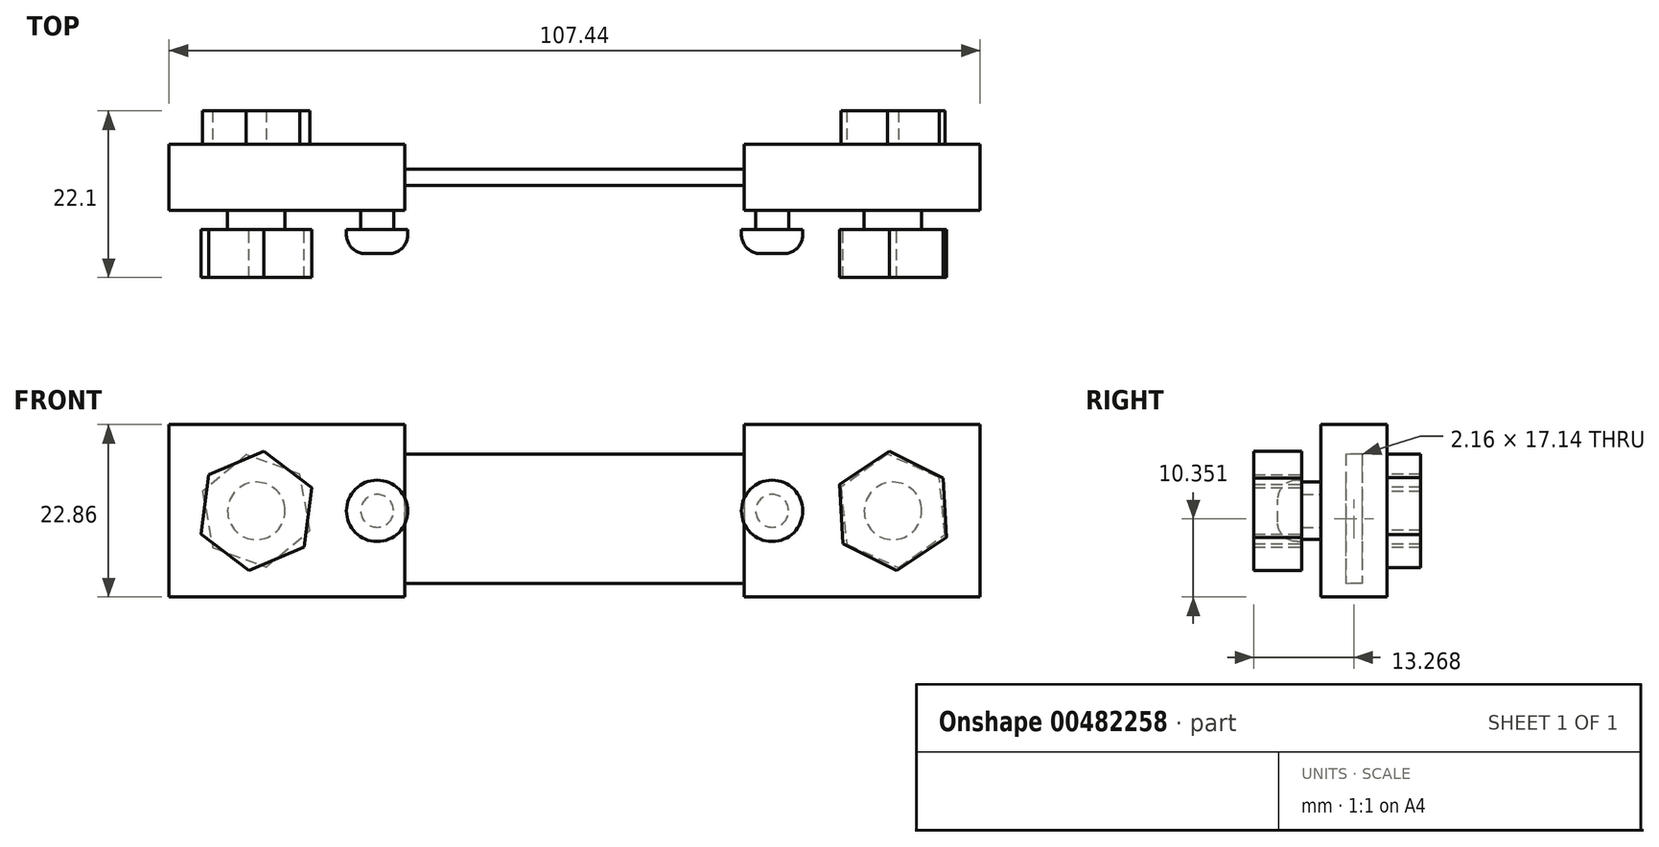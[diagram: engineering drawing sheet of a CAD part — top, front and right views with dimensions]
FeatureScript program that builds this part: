
annotation { "Feature Type Name" : "Feature", "Feature Type Description" : "" }
export const myFeature = defineFeature(function(context is Context, id is Id, definition is map)
    precondition{}
    {
        {
            var Q0;
            Q0=qCreatedBy(makeId("Front.planeOp"),FACE);
            var sketch = newSketch(context, id + "F0", { "sketchPlane" : qUnion([Q0])});
            skLineSegment(sketch, "E0.bottom", {"start": v(-53.72, 11.43) * mm, "end": v(53.72, 11.43) * mm});
            skLineSegment(sketch, "E0.top", {"start": v(-53.72, -11.43) * mm, "end": v(53.72, -11.43) * mm});
            skLineSegment(sketch, "E0.left", {"start": v(-53.72, 11.43) * mm, "end": v(-53.72, -11.43) * mm});
            skLineSegment(sketch, "E0.right", {"start": v(53.72, 11.43) * mm, "end": v(53.72, -11.43) * mm});
            skPoint(sketch, "E0.middle", {"position": v(0, 0) * mm});
            skSolve(sketch);
        }
        {
            var Q0;
            Q0 = qSketchRegion(id + "F0", true);
            extrude(context, id + "F1", {"entities" : qUnion([Q0]), "depth" : 8.76 * mm});
        }
        {
            var Q0;
            Q0=makeQuery(id+"F1.opExtrude","CAP_FACE",FACE,{"disambiguationData":[OSD([sQuery(id+"F0.wireOp",EDGE,"E0.bottom"),sQuery(id+"F0.wireOp",EDGE,"E0.top"),sQuery(id+"F0.wireOp",EDGE,"E0.left"),sQuery(id+"F0.wireOp",EDGE,"E0.right")])],"isStart":false});
            var sketch = newSketch(context, id + "F2", { "sketchPlane" : qUnion([Q0])});
            skLineSegment(sketch, "E1.bottom", {"start": v(22.48, 7.5) * mm, "end": v(-22.48, 7.5) * mm});
            skLineSegment(sketch, "E1.top", {"start": v(22.48, 14.3) * mm, "end": v(-22.48, 14.3) * mm});
            skLineSegment(sketch, "E1.left", {"start": v(22.48, 7.5) * mm, "end": v(22.48, 14.3) * mm});
            skLineSegment(sketch, "E1.right", {"start": v(-22.48, 7.5) * mm, "end": v(-22.48, 14.3) * mm});
            skPoint(sketch, "E1.middle", {"position": v(0, 10.9) * mm});
            skLineSegment(sketch, "E2.bottom", {"start": v(22.48, -9.65) * mm, "end": v(-22.48, -9.65) * mm});
            skLineSegment(sketch, "E2.top", {"start": v(22.48, -16.45) * mm, "end": v(-22.48, -16.45) * mm});
            skLineSegment(sketch, "E2.left", {"start": v(22.48, -9.65) * mm, "end": v(22.48, -16.45) * mm});
            skLineSegment(sketch, "E2.right", {"start": v(-22.48, -9.65) * mm, "end": v(-22.48, -16.45) * mm});
            skPoint(sketch, "E2.middle", {"position": v(0, -13.05) * mm});
            skLineSegment(sketch, "E3", {"start": v(-22.48, 7.5) * mm, "end": v(-22.48, -9.65) * mm, "construction": true});
            skSolve(sketch);
        }
        {
            var Q0;
            Q0 = qSketchRegion(id + "F2", true);
            extrude(context, id + "F3", {"entities" : qUnion([Q0]), "operationType" : NewBodyOperationType.REMOVE, "oppositeDirection" : true, "depth" : 25.4 * mm});
        }
        {
            var Q0;
            Q0=makeQuery(id+"F1.opExtrude","CAP_FACE",FACE,{"disambiguationData":[OSD([sQuery(id+"F0.wireOp",EDGE,"E0.bottom"),sQuery(id+"F0.wireOp",EDGE,"E0.top"),sQuery(id+"F0.wireOp",EDGE,"E0.left"),sQuery(id+"F0.wireOp",EDGE,"E0.right")])],"isStart":false});
            var sketch = newSketch(context, id + "F4", { "sketchPlane" : qUnion([Q0])});
            skLineSegment(sketch, "E4.bottom", {"start": v(-22.48, 7.5) * mm, "end": v(22.48, 7.5) * mm});
            skLineSegment(sketch, "E4.top", {"start": v(-22.48, -9.65) * mm, "end": v(22.48, -9.65) * mm});
            skLineSegment(sketch, "E4.left", {"start": v(-22.48, 7.5) * mm, "end": v(-22.48, -9.65) * mm});
            skLineSegment(sketch, "E4.right", {"start": v(22.48, 7.5) * mm, "end": v(22.48, -9.65) * mm});
            skSolve(sketch);
        }
        {
            var Q0;
            Q0 = qSketchRegion(id + "F4", true);
            extrude(context, id + "F5", {"entities" : qUnion([Q0]), "operationType" : NewBodyOperationType.REMOVE, "oppositeDirection" : true, "depth" : 3.3 * mm});
        }
        {
            var Q0;
            Q0=makeQuery(id+"F1.opExtrude","CAP_FACE",FACE,{"disambiguationData":[OSD([sQuery(id+"F0.wireOp",EDGE,"E0.bottom"),sQuery(id+"F0.wireOp",EDGE,"E0.top"),sQuery(id+"F0.wireOp",EDGE,"E0.left"),sQuery(id+"F0.wireOp",EDGE,"E0.right")])],"isStart":true});
            var sketch = newSketch(context, id + "F6", { "sketchPlane" : qUnion([Q0])});
            skLineSegment(sketch, "E5.bottom", {"start": v(-22.48, 7.5) * mm, "end": v(22.48, 7.5) * mm});
            skLineSegment(sketch, "E5.top", {"start": v(-22.48, -9.65) * mm, "end": v(22.48, -9.65) * mm});
            skLineSegment(sketch, "E5.left", {"start": v(-22.48, 7.5) * mm, "end": v(-22.48, -9.65) * mm});
            skLineSegment(sketch, "E5.right", {"start": v(22.48, 7.5) * mm, "end": v(22.48, -9.65) * mm});
            skSolve(sketch);
        }
        {
            var Q0;
            Q0 = qSketchRegion(id + "F6", true);
            extrude(context, id + "F7", {"entities" : qUnion([Q0]), "operationType" : NewBodyOperationType.REMOVE, "oppositeDirection" : true, "depth" : 3.3 * mm});
        }
        {
            var Q0;
            {var subQ0=sQuery(id+"F0.wireOp",EDGE,"E0.left");var subQ1=sQuery(id+"F0.wireOp",EDGE,"E0.top");var subQ2=sQuery(id+"F0.wireOp",EDGE,"E0.bottom");Q0=makeQuery(id+"F5.boolean.opBoolean","SPLIT",FACE,{"disambiguationData":[TD([makeQuery(id+"F1.opExtrude","SWEPT_FACE",FACE,{"disambiguationData":[OSD([subQ0])]})])],"derivedFrom":makeQuery(id+"F1.opExtrude","CAP_FACE",FACE,{"disambiguationData":[OSD([subQ2,subQ1,subQ0,sQuery(id+"F0.wireOp",EDGE,"E0.right")])],"isStart":false})});}
            var sketch = newSketch(context, id + "F8", { "sketchPlane" : qUnion([Q0])});
            skCircle(sketch, "E6", {"center": v(-26.16, 0) * mm, "radius": 2.17 * mm});
            skPoint(sketch, "E6.centerSnap0", {"position": v(-22.48, 0) * mm});
            skCircle(sketch, "E7", {"center": v(26.16, 0) * mm, "radius": 2.17 * mm});
            skCircle(sketch, "E8", {"center": v(42.16, 0) * mm, "radius": 3.81 * mm});
            skCircle(sketch, "E9", {"center": v(-42.16, 0) * mm, "radius": 3.81 * mm});
            skLineSegment(sketch, "E10", {"start": v(-42.16, 0) * mm, "end": v(-26.16, 0) * mm, "construction": true});
            skLineSegment(sketch, "E11", {"start": v(26.16, 0) * mm, "end": v(42.16, 0) * mm, "construction": true});
            skLineSegment(sketch, "E12", {"start": v(26.16, 0) * mm, "end": v(-26.16, 0) * mm, "construction": true});
            skSolve(sketch);
        }
        {
            var Q0;
            Q0 = qSketchRegion(id + "F8", true);
            extrude(context, id + "F9", {"entities" : qUnion([Q0]), "operationType" : NewBodyOperationType.ADD, "depth" : 2.54 * mm});
        }
        {
            var Q0;
            Q0=makeQuery(id+"F9.opExtrude","CAP_FACE",FACE,{"disambiguationData":[OSD([sQuery(id+"F8.wireOp",EDGE,"E6")])],"isStart":false});
            var sketch = newSketch(context, id + "F10", { "sketchPlane" : qUnion([Q0])});
            skCircle(sketch, "E13", {"center": v(-26.16, 0) * mm, "radius": 4.06 * mm});
            skCircle(sketch, "E14", {"center": v(26.16, 0) * mm, "radius": 4.06 * mm});
            skSolve(sketch);
        }
        {
            var Q0;
            Q0 = qSketchRegion(id + "F10", true);
            extrude(context, id + "F11", {"entities" : qUnion([Q0]), "operationType" : NewBodyOperationType.ADD, "depth" : 3.17 * mm});
        }
        {
            var Q0;
            Q0=makeQuery(id+"F11.opExtrude","CAP_FACE",FACE,{"disambiguationData":[OSD([sQuery(id+"F10.wireOp",EDGE,"E13")])],"isStart":false});
            var Q1;
            Q1=makeQuery(id+"F11.opExtrude","CAP_FACE",FACE,{"disambiguationData":[OSD([sQuery(id+"F10.wireOp",EDGE,"E14")])],"isStart":false});
            fillet(context, id + "F12", {"entities" : qUnion([Q0, Q1]), "radius" : 2.54 * mm, "tangentPropagation" : true, "allowEdgeOverflow" : false});
        }
        {
            var Q0;
            Q0=makeQuery(id+"F9.opExtrude","CAP_FACE",FACE,{"disambiguationData":[OSD([sQuery(id+"F8.wireOp",EDGE,"E9")])],"isStart":false});
            var sketch = newSketch(context, id + "F13", { "sketchPlane" : qUnion([Q0])});
            skCircle(sketch, "E15.cCircle", {"center": v(-42.16, 0) * mm, "radius": 7.94 * mm, "construction": true});
            skLineSegment(sketch, "E15.0", {"start": v(-41.18, 7.88) * mm, "end": v(-34.85, 3.08) * mm});
            skLineSegment(sketch, "E15.1", {"start": v(-34.85, 3.08) * mm, "end": v(-35.84, -4.8) * mm});
            skLineSegment(sketch, "E15.2", {"start": v(-35.84, -4.8) * mm, "end": v(-43.15, -7.88) * mm});
            skLineSegment(sketch, "E15.3", {"start": v(-43.15, -7.88) * mm, "end": v(-49.48, -3.08) * mm});
            skLineSegment(sketch, "E15.4", {"start": v(-49.48, -3.08) * mm, "end": v(-48.5, 4.8) * mm});
            skLineSegment(sketch, "E15.5", {"start": v(-48.5, 4.8) * mm, "end": v(-41.18, 7.88) * mm});
            skCircle(sketch, "E16.cCircle", {"center": v(42.16, 0) * mm, "radius": 7.94 * mm, "construction": true});
            skLineSegment(sketch, "E16.0", {"start": v(41.7, 7.92) * mm, "end": v(48.79, 4.37) * mm});
            skLineSegment(sketch, "E16.1", {"start": v(48.79, 4.37) * mm, "end": v(49.26, -3.55) * mm});
            skLineSegment(sketch, "E16.2", {"start": v(49.26, -3.55) * mm, "end": v(42.64, -7.92) * mm});
            skLineSegment(sketch, "E16.3", {"start": v(42.64, -7.92) * mm, "end": v(35.54, -4.37) * mm});
            skLineSegment(sketch, "E16.4", {"start": v(35.54, -4.37) * mm, "end": v(35.07, 3.55) * mm});
            skLineSegment(sketch, "E16.5", {"start": v(35.07, 3.55) * mm, "end": v(41.7, 7.92) * mm});
            skSolve(sketch);
        }
        {
            var Q0;
            Q0 = qSketchRegion(id + "F13", true);
            extrude(context, id + "F14", {"entities" : qUnion([Q0]), "operationType" : NewBodyOperationType.ADD, "depth" : 6.35 * mm});
        }
        {
            var Q0;
            {var subQ0=sQuery(id+"F0.wireOp",EDGE,"E0.left");var subQ1=sQuery(id+"F0.wireOp",EDGE,"E0.top");var subQ2=sQuery(id+"F0.wireOp",EDGE,"E0.bottom");Q0=makeQuery(id+"F7.boolean.opBoolean","SPLIT",FACE,{"disambiguationData":[TD([makeQuery(id+"F1.opExtrude","SWEPT_FACE",FACE,{"disambiguationData":[OSD([subQ0])]})])],"derivedFrom":makeQuery(id+"F1.opExtrude","CAP_FACE",FACE,{"disambiguationData":[OSD([subQ2,subQ1,subQ0,sQuery(id+"F0.wireOp",EDGE,"E0.right")])],"isStart":true})});}
            var sketch = newSketch(context, id + "F15", { "sketchPlane" : qUnion([Q0])});
            skCircle(sketch, "E17.0", {"center": v(42.16, 0) * mm, "radius": 3.81 * mm, "construction": true});
            skCircle(sketch, "E18.0", {"center": v(-42.16, 0) * mm, "radius": 3.81 * mm, "construction": true});
            skCircle(sketch, "E19.cCircle", {"center": v(-42.16, 0) * mm, "radius": 7.56 * mm, "construction": true});
            skLineSegment(sketch, "E19.0", {"start": v(-41.42, 7.52) * mm, "end": v(-35.28, 3.12) * mm});
            skLineSegment(sketch, "E19.1", {"start": v(-35.28, 3.12) * mm, "end": v(-36.02, -4.4) * mm});
            skLineSegment(sketch, "E19.2", {"start": v(-36.02, -4.4) * mm, "end": v(-42.9, -7.52) * mm});
            skLineSegment(sketch, "E19.3", {"start": v(-42.9, -7.52) * mm, "end": v(-49.05, -3.12) * mm});
            skLineSegment(sketch, "E19.4", {"start": v(-49.05, -3.12) * mm, "end": v(-48.3, 4.4) * mm});
            skLineSegment(sketch, "E19.5", {"start": v(-48.3, 4.4) * mm, "end": v(-41.42, 7.52) * mm});
            skCircle(sketch, "E20.cCircle", {"center": v(42.16, 0) * mm, "radius": 7.56 * mm, "construction": true});
            skLineSegment(sketch, "E20.0", {"start": v(43.5, 7.44) * mm, "end": v(49.27, 2.56) * mm});
            skLineSegment(sketch, "E20.1", {"start": v(49.27, 2.56) * mm, "end": v(47.93, -4.88) * mm});
            skLineSegment(sketch, "E20.2", {"start": v(47.93, -4.88) * mm, "end": v(40.82, -7.44) * mm});
            skLineSegment(sketch, "E20.3", {"start": v(40.82, -7.44) * mm, "end": v(35.05, -2.56) * mm});
            skLineSegment(sketch, "E20.4", {"start": v(35.05, -2.56) * mm, "end": v(36.4, 4.88) * mm});
            skLineSegment(sketch, "E20.5", {"start": v(36.4, 4.88) * mm, "end": v(43.5, 7.44) * mm});
            skSolve(sketch);
        }
        {
            var Q0;
            Q0 = qSketchRegion(id + "F15", true);
            extrude(context, id + "F16", {"entities" : qUnion([Q0]), "operationType" : NewBodyOperationType.ADD, "depth" : 4.44 * mm});
        }
    });
